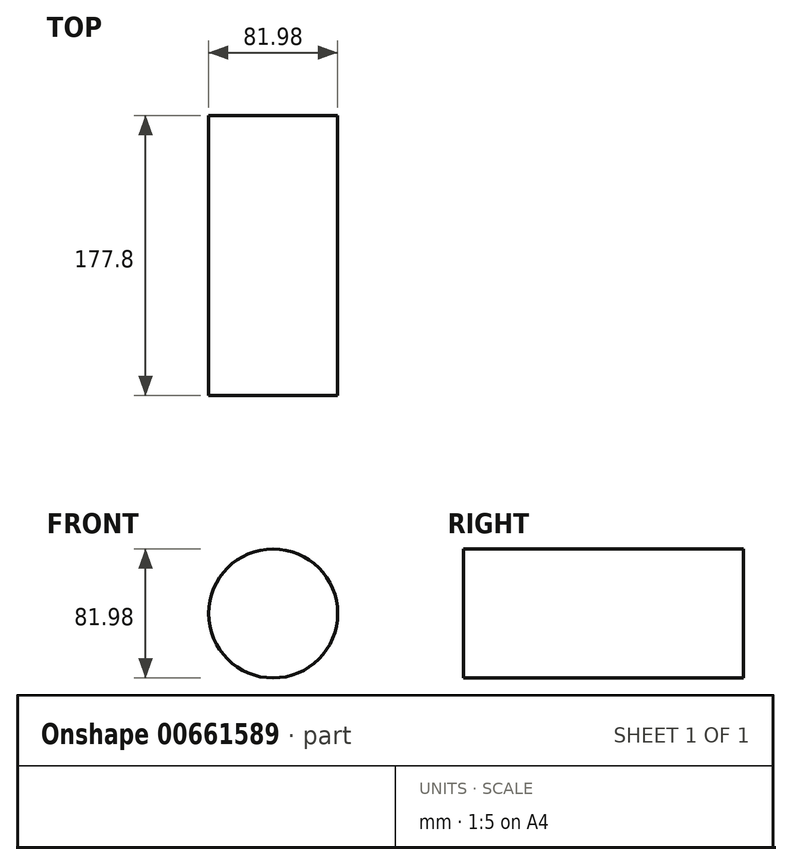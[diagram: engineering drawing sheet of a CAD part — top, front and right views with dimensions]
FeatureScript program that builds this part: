
annotation { "Feature Type Name" : "Feature", "Feature Type Description" : "" }
export const myFeature = defineFeature(function(context is Context, id is Id, definition is map)
    precondition{}
    {
        {
            var Q0;
            Q0=qCreatedBy(makeId("Front.planeOp"),FACE);
            var sketch = newSketch(context, id + "F0", { "sketchPlane" : qUnion([Q0])});
            skCircle(sketch, "E0", {"center": v(0, 0) * mm, "radius": 41 * mm});
            skSolve(sketch);
        }
        {
            var Q0;
            Q0=makeQuery(id+"F0.imprint","IMPRINT",FACE,{"disambiguationData":[TD([[makeQuery(id+"F0.imprint","IMPRINT",EDGE,{"derivedFrom":sQuery(id+"F0.wireOp",EDGE,"E0")}),1.0]])]});
            extrude(context, id + "F1", {"entities" : qUnion([Q0]), "depth" : 177.8 * mm, "offsetDistance" : 25.4 * mm});
        }
    });
